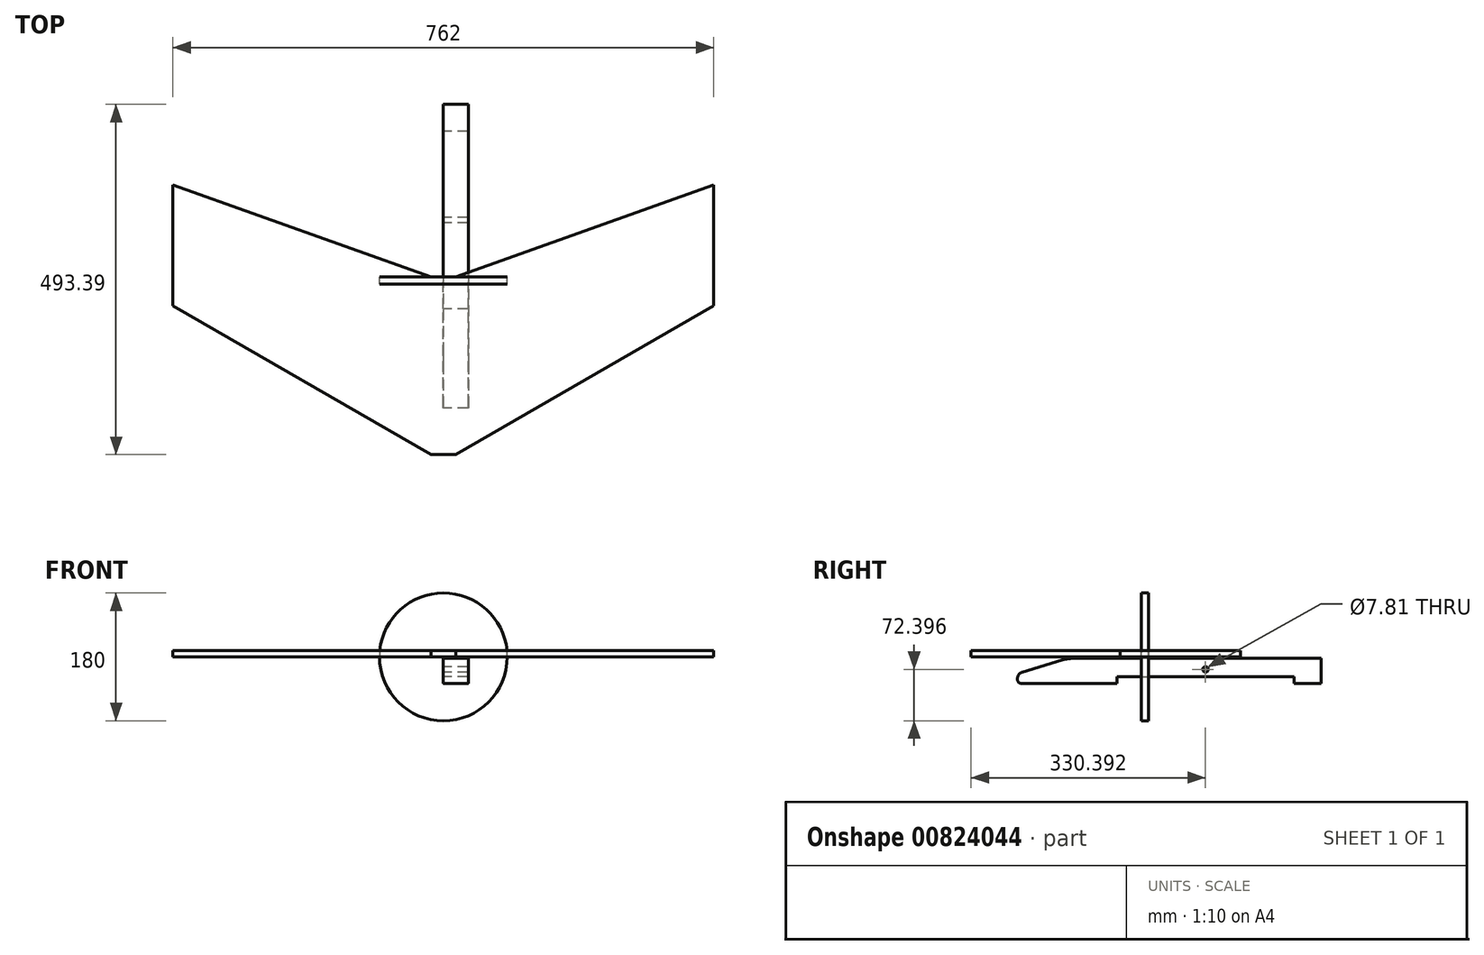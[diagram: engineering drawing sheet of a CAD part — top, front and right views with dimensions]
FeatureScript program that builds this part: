
annotation { "Feature Type Name" : "Feature", "Feature Type Description" : "" }
export const myFeature = defineFeature(function(context is Context, id is Id, definition is map)
    precondition{}
    {
        {
            var Q0;
            Q0=qCreatedBy(makeId("Top.planeOp"),FACE);
            var sketch = newSketch(context, id + "F0", { "sketchPlane" : qUnion([Q0])});
            skLineSegment(sketch, "E0", {"start": v(-381, 129.87) * mm, "end": v(-381, -40.13) * mm});
            skLineSegment(sketch, "E1", {"start": v(-381, -40.13) * mm, "end": v(-17.5, -250) * mm});
            skLineSegment(sketch, "E2", {"start": v(-17.5, -250) * mm, "end": v(17.5, -250) * mm});
            skLineSegment(sketch, "E3", {"start": v(17.5, -250) * mm, "end": v(381, -40.13) * mm});
            skLineSegment(sketch, "E4", {"start": v(381, -40.13) * mm, "end": v(381, 129.87) * mm});
            skLineSegment(sketch, "E5", {"start": v(-381, 129.87) * mm, "end": v(-17.5, 0) * mm});
            skLineSegment(sketch, "E6", {"start": v(-17.5, 0) * mm, "end": v(0, 0) * mm});
            skLineSegment(sketch, "E7", {"start": v(17.5, 0) * mm, "end": v(381, 129.87) * mm});
            skLineSegment(sketch, "E8", {"start": v(0, 0) * mm, "end": v(17.5, 0) * mm});
            skSolve(sketch);
        }
        {
            var Q0;
            Q0=makeQuery(id+"F0.imprint","IMPRINT",FACE,{"disambiguationData":[TD([[makeQuery(id+"F0.imprint","IMPRINT",EDGE,{"derivedFrom":sQuery(id+"F0.wireOp",EDGE,"E0")}),1.0]])]});
            extrude(context, id + "F1", {"entities" : qUnion([Q0]), "depth" : 9 * mm, "offsetDistance" : 25 * mm});
        }
        {
            var Q0;
            Q0=qCreatedBy(makeId("Front.planeOp"),FACE);
            var sketch = newSketch(context, id + "F2", { "sketchPlane" : qUnion([Q0])});
            skCircle(sketch, "E9", {"center": v(0, 0) * mm, "radius": 90 * mm});
            skSolve(sketch);
        }
        {
            var Q0;
            Q0 = qSketchRegion(id + "F2", true);
            extrude(context, id + "F3", {"entities" : qUnion([Q0]), "depth" : 10 * mm, "offsetDistance" : 25 * mm});
        }
        {
            var Q0;
            Q0=qCreatedBy(makeId("Right.planeOp"),FACE);
            var sketch = newSketch(context, id + "F4", { "sketchPlane" : qUnion([Q0])});
            skLineSegment(sketch, "E10", {"start": v(-44.6, -37.25) * mm, "end": v(-44.6, -28.25) * mm});
            skLineSegment(sketch, "E11", {"start": v(-44.6, -28.25) * mm, "end": v(80.4, -28.25) * mm});
            skLineSegment(sketch, "E12", {"start": v(205.4, -28.25) * mm, "end": v(205.4, -37.25) * mm});
            skLineSegment(sketch, "E13", {"start": v(205.4, -37.25) * mm, "end": v(243.4, -37.25) * mm});
            skLineSegment(sketch, "E14", {"start": v(243.4, -37.25) * mm, "end": v(243.4, -2.25) * mm});
            skLineSegment(sketch, "E15", {"start": v(243.4, -2.25) * mm, "end": v(-107.2, -2.25) * mm});
            skLineSegment(sketch, "E16", {"start": v(-114.6, -37.25) * mm, "end": v(-44.6, -37.25) * mm});
            skLineSegment(sketch, "E17", {"start": v(-121.7, -4.4) * mm, "end": v(-177.5, -21.32) * mm});
            skLineSegment(sketch, "E18", {"start": v(-184.6, -30.89) * mm, "end": v(-184.6, -32.25) * mm});
            skLineSegment(sketch, "E19", {"start": v(-179.6, -37.25) * mm, "end": v(-114.6, -37.25) * mm});
            skPoint(sketch, "E20.visualSharp", {"position": v(-184.6, -23.47) * mm});
            skArc(sketch, "E20.filletArc", {"start": v(-177.5, -21.32) * mm, "mid": v(-182.64, -24.93) * mm, "end": v(-184.6, -30.89) * mm});
            skLineSegment(sketch, "E21", {"start": v(80.4, -28.25) * mm, "end": v(205.4, -28.25) * mm});
            skCircle(sketch, "E22", {"center": v(80.4, -17.6) * mm, "radius": 3.9 * mm});
            skPoint(sketch, "E23.visualSharp", {"position": v(-114.6, -2.25) * mm});
            skArc(sketch, "E23.filletArc", {"start": v(-107.2, -2.25) * mm, "mid": v(-114.53, -2.79) * mm, "end": v(-121.7, -4.4) * mm});
            skPoint(sketch, "E24.visualSharp", {"position": v(-184.6, -37.25) * mm});
            skArc(sketch, "E24.filletArc", {"start": v(-184.6, -32.25) * mm, "mid": v(-183.14, -35.78) * mm, "end": v(-179.6, -37.25) * mm});
            skSolve(sketch);
        }
        {
            var Q0;
            Q0 = qSketchRegion(id + "F4", true);
            extrude(context, id + "F5", {"entities" : qUnion([Q0]), "depth" : 35 * mm, "offsetDistance" : 25 * mm});
        }
    });
